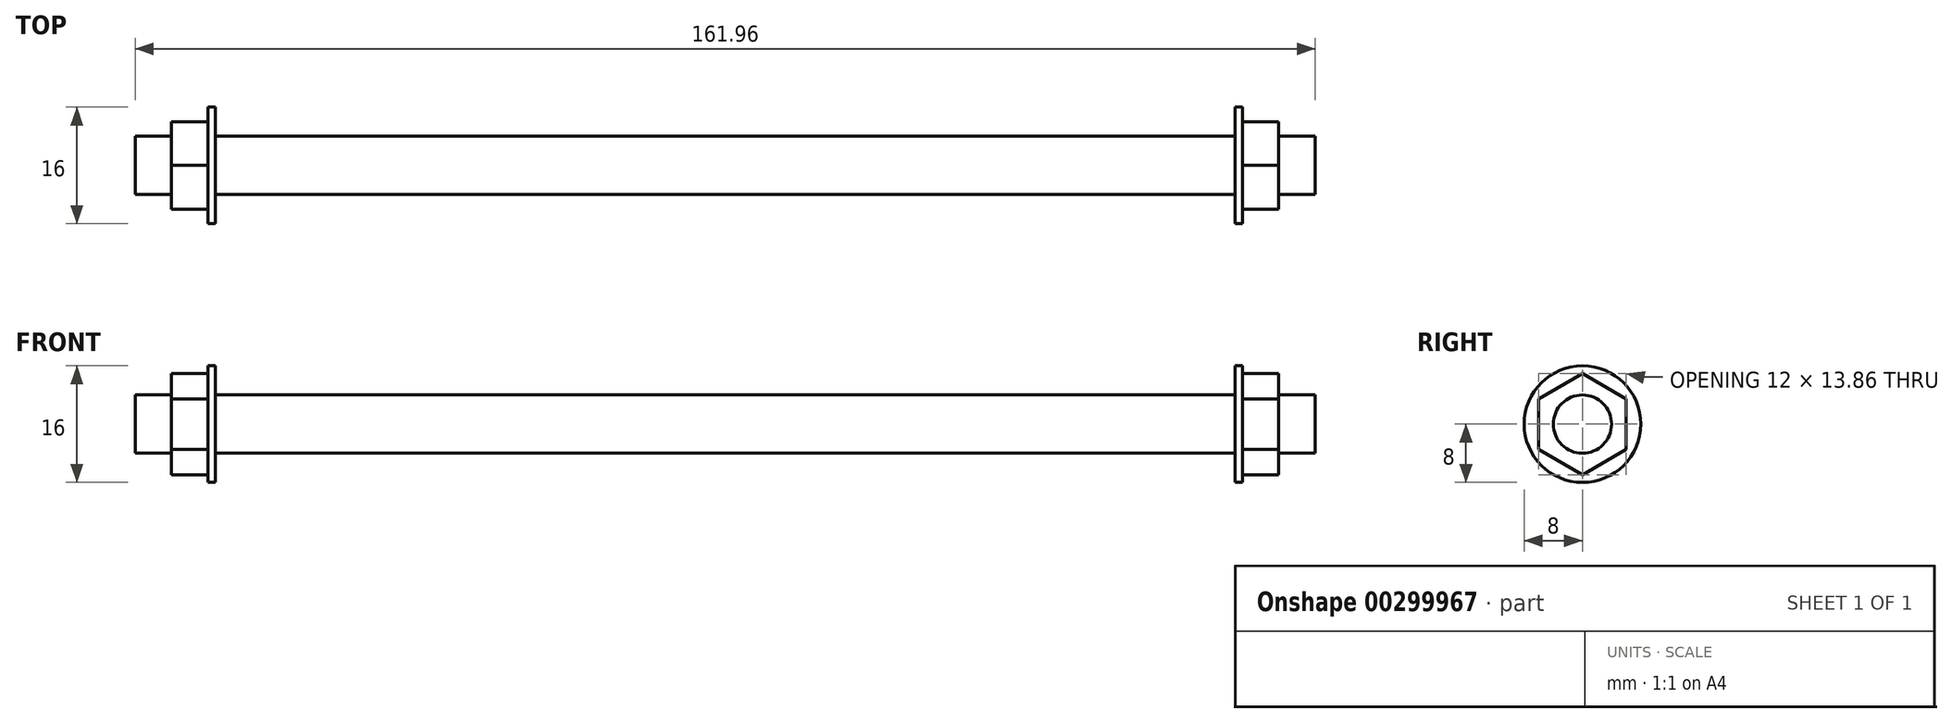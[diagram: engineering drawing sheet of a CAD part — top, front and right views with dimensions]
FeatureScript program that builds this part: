
annotation { "Feature Type Name" : "Feature", "Feature Type Description" : "" }
export const myFeature = defineFeature(function(context is Context, id is Id, definition is map)
    precondition{}
    {
        {
            var Q0;
            Q0=qCreatedBy(makeId("Right.planeOp"),FACE);
            var sketch = newSketch(context, id + "F0", { "sketchPlane" : qUnion([Q0])});
            skCircle(sketch, "E0", {"center": v(0, 0) * mm, "radius": 4 * mm});
            skSolve(sketch);
        }
        {
            var Q0;
            Q0 = qSketchRegion(id + "F0", true);
            extrude(context, id + "F1", {"entities" : qUnion([Q0]), "endBound" : BoundingType.SYMMETRIC, "depth" : 139.95 * mm, "offsetDistance" : 25.4 * mm});
        }
        {
            var Q0;
            Q0=makeQuery(id+"F1.opExtrude","CAP_FACE",FACE,{"disambiguationData":[OSD([sQuery(id+"F0.wireOp",EDGE,"E0")])],"isStart":false});
            var sketch = newSketch(context, id + "F2", { "sketchPlane" : qUnion([Q0])});
            skCircle(sketch, "E1", {"center": v(0, 0) * mm, "radius": 8 * mm});
            skSolve(sketch);
        }
        {
            var Q0;
            Q0 = qSketchRegion(id + "F2", true);
            extrude(context, id + "F3", {"entities" : qUnion([Q0]), "operationType" : NewBodyOperationType.ADD, "depth" : 1 * mm});
        }
        {
            var Q0;
            Q0=makeQuery(id+"F3.opExtrude","CAP_FACE",FACE,{"disambiguationData":[OSD([sQuery(id+"F2.wireOp",EDGE,"E1")])],"isStart":false});
            var sketch = newSketch(context, id + "F4", { "sketchPlane" : qUnion([Q0])});
            skCircle(sketch, "E2.cCircle", {"center": v(0, 0) * mm, "radius": 6 * mm, "construction": true});
            skLineSegment(sketch, "E2.0", {"start": v(0, 6.93) * mm, "end": v(6, 3.46) * mm});
            skLineSegment(sketch, "E2.1", {"start": v(6, 3.46) * mm, "end": v(6, -3.46) * mm});
            skLineSegment(sketch, "E2.2", {"start": v(6, -3.46) * mm, "end": v(0, -6.93) * mm});
            skLineSegment(sketch, "E2.3", {"start": v(0, -6.93) * mm, "end": v(-6, -3.46) * mm});
            skLineSegment(sketch, "E2.4", {"start": v(-6, -3.46) * mm, "end": v(-6, 3.46) * mm});
            skLineSegment(sketch, "E2.5", {"start": v(-6, 3.46) * mm, "end": v(0, 6.93) * mm});
            skPoint(sketch, "E2.0.midPoint", {"position": v(3, 5.2) * mm});
            skSolve(sketch);
        }
        {
            var Q0;
            Q0 = qSketchRegion(id + "F4", true);
            extrude(context, id + "F5", {"entities" : qUnion([Q0]), "operationType" : NewBodyOperationType.ADD, "depth" : 5 * mm});
        }
        {
            var Q0;
            Q0=makeQuery(id+"F5.opExtrude","CAP_FACE",FACE,{"disambiguationData":[OSD([sQuery(id+"F4.wireOp",EDGE,"E2.0"),sQuery(id+"F4.wireOp",EDGE,"E2.1"),sQuery(id+"F4.wireOp",EDGE,"E2.2"),sQuery(id+"F4.wireOp",EDGE,"E2.3"),sQuery(id+"F4.wireOp",EDGE,"E2.4"),sQuery(id+"F4.wireOp",EDGE,"E2.5")])],"isStart":false});
            var sketch = newSketch(context, id + "F6", { "sketchPlane" : qUnion([Q0])});
            skCircle(sketch, "E3", {"center": v(0, 0) * mm, "radius": 4 * mm});
            skSolve(sketch);
        }
        {
            var Q0;
            Q0 = qSketchRegion(id + "F6", true);
            extrude(context, id + "F7", {"entities" : qUnion([Q0]), "operationType" : NewBodyOperationType.ADD, "depth" : 5 * mm});
        }
        {
            var Q0;
            Q0=makeQuery(id+"F1.opExtrude","CAP_FACE",FACE,{"disambiguationData":[OSD([sQuery(id+"F0.wireOp",EDGE,"E0")])],"isStart":true});
            var sketch = newSketch(context, id + "F8", { "sketchPlane" : qUnion([Q0])});
            skCircle(sketch, "E4", {"center": v(0, 0) * mm, "radius": 8 * mm});
            skSolve(sketch);
        }
        {
            var Q0;
            Q0 = qSketchRegion(id + "F8", true);
            extrude(context, id + "F9", {"entities" : qUnion([Q0]), "operationType" : NewBodyOperationType.ADD, "depth" : 1 * mm});
        }
        {
            var Q0;
            Q0=makeQuery(id+"F9.opExtrude","CAP_FACE",FACE,{"disambiguationData":[OSD([sQuery(id+"F8.wireOp",EDGE,"E4")])],"isStart":false});
            var sketch = newSketch(context, id + "F10", { "sketchPlane" : qUnion([Q0])});
            skCircle(sketch, "E5.cCircle", {"center": v(0, 0) * mm, "radius": 6 * mm, "construction": true});
            skLineSegment(sketch, "E5.0", {"start": v(6, -3.46) * mm, "end": v(0, -6.93) * mm});
            skLineSegment(sketch, "E5.1", {"start": v(0, -6.93) * mm, "end": v(-6, -3.46) * mm});
            skLineSegment(sketch, "E5.2", {"start": v(-6, -3.46) * mm, "end": v(-6, 3.46) * mm});
            skLineSegment(sketch, "E5.3", {"start": v(-6, 3.46) * mm, "end": v(0, 6.93) * mm});
            skLineSegment(sketch, "E5.4", {"start": v(0, 6.93) * mm, "end": v(6, 3.46) * mm});
            skLineSegment(sketch, "E5.5", {"start": v(6, 3.46) * mm, "end": v(6, -3.46) * mm});
            skPoint(sketch, "E5.0.midPoint", {"position": v(3, -5.2) * mm});
            skSolve(sketch);
        }
        {
            var Q0;
            Q0 = qSketchRegion(id + "F10", true);
            extrude(context, id + "F11", {"entities" : qUnion([Q0]), "operationType" : NewBodyOperationType.ADD, "depth" : 5 * mm});
        }
        {
            var Q0;
            Q0=makeQuery(id+"F11.opExtrude","CAP_FACE",FACE,{"disambiguationData":[OSD([sQuery(id+"F10.wireOp",EDGE,"E5.0"),sQuery(id+"F10.wireOp",EDGE,"E5.1"),sQuery(id+"F10.wireOp",EDGE,"E5.2"),sQuery(id+"F10.wireOp",EDGE,"E5.3"),sQuery(id+"F10.wireOp",EDGE,"E5.4"),sQuery(id+"F10.wireOp",EDGE,"E5.5")])],"isStart":false});
            var sketch = newSketch(context, id + "F12", { "sketchPlane" : qUnion([Q0])});
            skCircle(sketch, "E6", {"center": v(0, 0) * mm, "radius": 4 * mm});
            skSolve(sketch);
        }
        {
            var Q0;
            Q0 = qSketchRegion(id + "F12", true);
            extrude(context, id + "F13", {"entities" : qUnion([Q0]), "operationType" : NewBodyOperationType.ADD, "depth" : 5 * mm});
        }
    });
